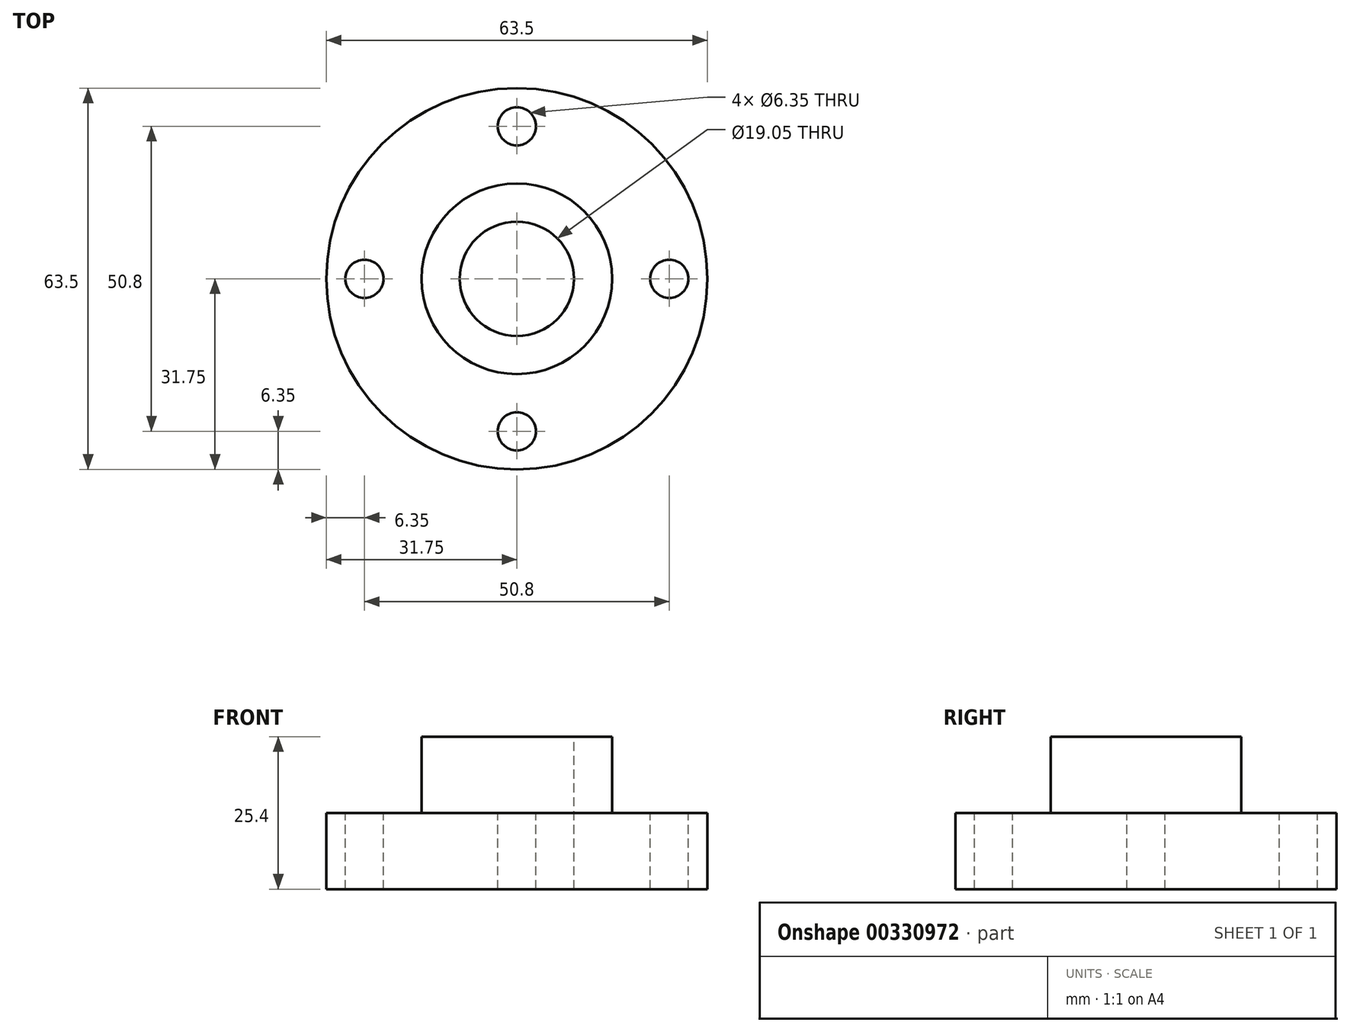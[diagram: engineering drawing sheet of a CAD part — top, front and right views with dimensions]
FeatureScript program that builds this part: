
annotation { "Feature Type Name" : "Feature", "Feature Type Description" : "" }
export const myFeature = defineFeature(function(context is Context, id is Id, definition is map)
    precondition{}
    {
        {
            var Q0;
            Q0=qCreatedBy(makeId("Top.planeOp"),FACE);
            var sketch = newSketch(context, id + "F0", { "sketchPlane" : qUnion([Q0])});
            skCircle(sketch, "E0", {"center": v(0, 0) * mm, "radius": 15.88 * mm});
            skCircle(sketch, "E1", {"center": v(0, 0) * mm, "radius": 9.53 * mm});
            skCircle(sketch, "E2", {"center": v(0, 0) * mm, "radius": 31.75 * mm});
            skCircle(sketch, "E3", {"center": v(-25.4, 0) * mm, "radius": 3.18 * mm});
            skCircle(sketch, "E4.1.0", {"center": v(0, -25.4) * mm, "radius": 3.18 * mm});
            skCircle(sketch, "E4.2.0", {"center": v(25.4, 0) * mm, "radius": 3.18 * mm});
            skCircle(sketch, "E4.3.0", {"center": v(0, 25.4) * mm, "radius": 3.18 * mm});
            skSolve(sketch);
        }
        {
            var Q0;
            Q0=makeQuery(id+"F0.imprint","IMPRINT",FACE,{"disambiguationData":[TD([[makeQuery(id+"F0.imprint","IMPRINT",EDGE,{"derivedFrom":sQuery(id+"F0.wireOp",EDGE,"E0")}),-1.0]])]});
            var Q1;
            Q1=makeQuery(id+"F0.imprint","IMPRINT",FACE,{"disambiguationData":[TD([[makeQuery(id+"F0.imprint","IMPRINT",EDGE,{"derivedFrom":sQuery(id+"F0.wireOp",EDGE,"E0")}),1.0]])]});
            extrude(context, id + "F1", {"entities" : qUnion([Q0, Q1]), "oppositeDirection" : true, "depth" : 12.7 * mm});
        }
        {
            var Q0;
            Q0=makeQuery(id+"F0.imprint","IMPRINT",FACE,{"disambiguationData":[TD([[makeQuery(id+"F0.imprint","IMPRINT",EDGE,{"derivedFrom":sQuery(id+"F0.wireOp",EDGE,"E0")}),1.0]])]});
            extrude(context, id + "F2", {"entities" : qUnion([Q0]), "operationType" : NewBodyOperationType.ADD, "depth" : 12.7 * mm});
        }
    });
